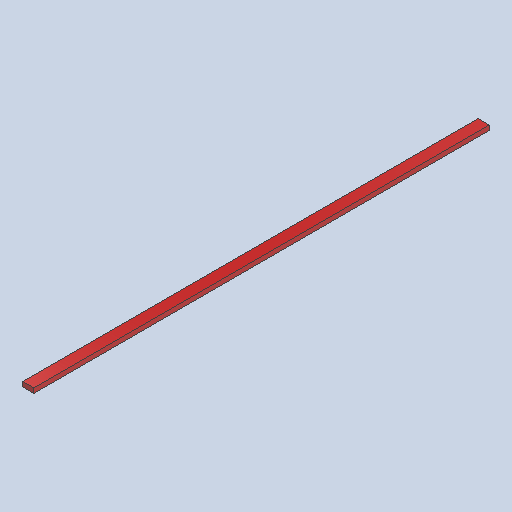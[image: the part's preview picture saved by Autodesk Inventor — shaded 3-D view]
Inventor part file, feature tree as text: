
AUTODESK INVENTOR PART (.ipt)
format: ipt  version: 2025.1 (Build 291241020, 241B)  size: 139,776 bytes
history: native  units: in
note: dims shown in document units (in); Inventor stores cm internally (conversion verified against a paired STEP export)
features: extrude x1, sketch x1, other x1
ambient origin geometry x8: Origin, YZ Plane, XZ Plane, XY Plane, X Axis, Y Axis, Z Axis, Center Point
bodies: Solid1 (feature_tree)
feature tree (3):
  extrude  "Extrusion1"  Depth=1.5in
  sketch  "Sketch1"  dims[d0=3.5in d1=1.5in d2=144.0in d3=0.0in]
  other  "Finish1"
